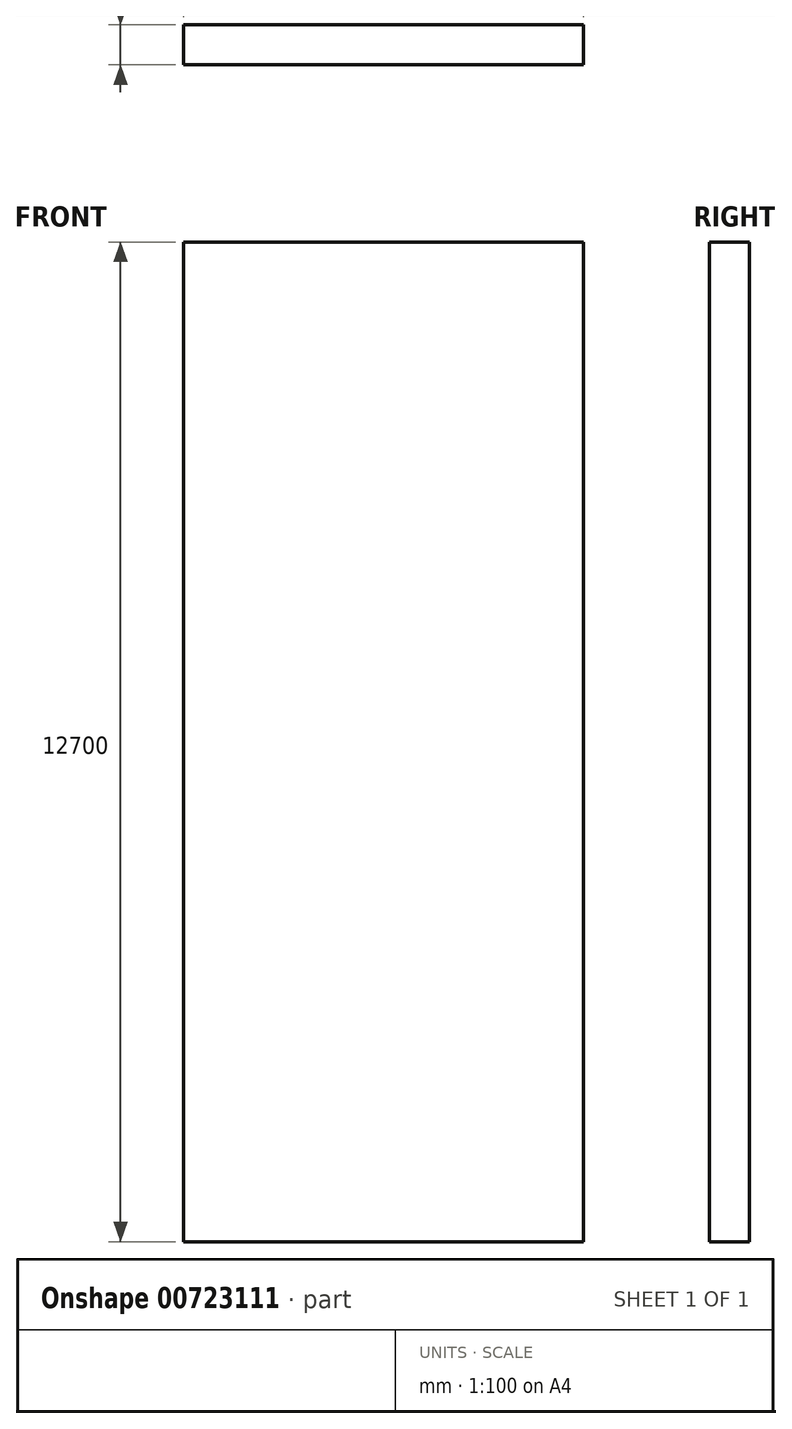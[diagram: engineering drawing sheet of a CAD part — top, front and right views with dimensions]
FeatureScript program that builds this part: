
annotation { "Feature Type Name" : "Feature", "Feature Type Description" : "" }
export const myFeature = defineFeature(function(context is Context, id is Id, definition is map)
    precondition{}
    {
        {
            var Q0;
            Q0=qCreatedBy(makeId("Front.planeOp"),FACE);
            var sketch = newSketch(context, id + "F0", { "sketchPlane" : qUnion([Q0])});
            skLineSegment(sketch, "E0.bottom", {"start": v(-2540, 6350) * mm, "end": v(2540, 6350) * mm});
            skLineSegment(sketch, "E0.top", {"start": v(-2540, -6350) * mm, "end": v(2540, -6350) * mm});
            skLineSegment(sketch, "E0.left", {"start": v(-2540, 6350) * mm, "end": v(-2540, -6350) * mm});
            skLineSegment(sketch, "E0.right", {"start": v(2540, 6350) * mm, "end": v(2540, -6350) * mm});
            skLineSegment(sketch, "E1.0", {"start": v(-2540, 4470.4) * mm, "end": v(2540, 4470.4) * mm});
            skLineSegment(sketch, "E2", {"start": v(-2540, 6350) * mm, "end": v(2540, -6350) * mm, "construction": true});
            skLineSegment(sketch, "E3", {"start": v(2540, 6350) * mm, "end": v(-2540, -6350) * mm, "construction": true});
            skSolve(sketch);
        }
        {
            var Q0;
            Q0 = qSketchRegion(id + "F0", true);
            extrude(context, id + "F1", {"entities" : qUnion([Q0]), "depth" : 508 * mm, "offsetDistance" : 25.4 * mm});
        }
    });
